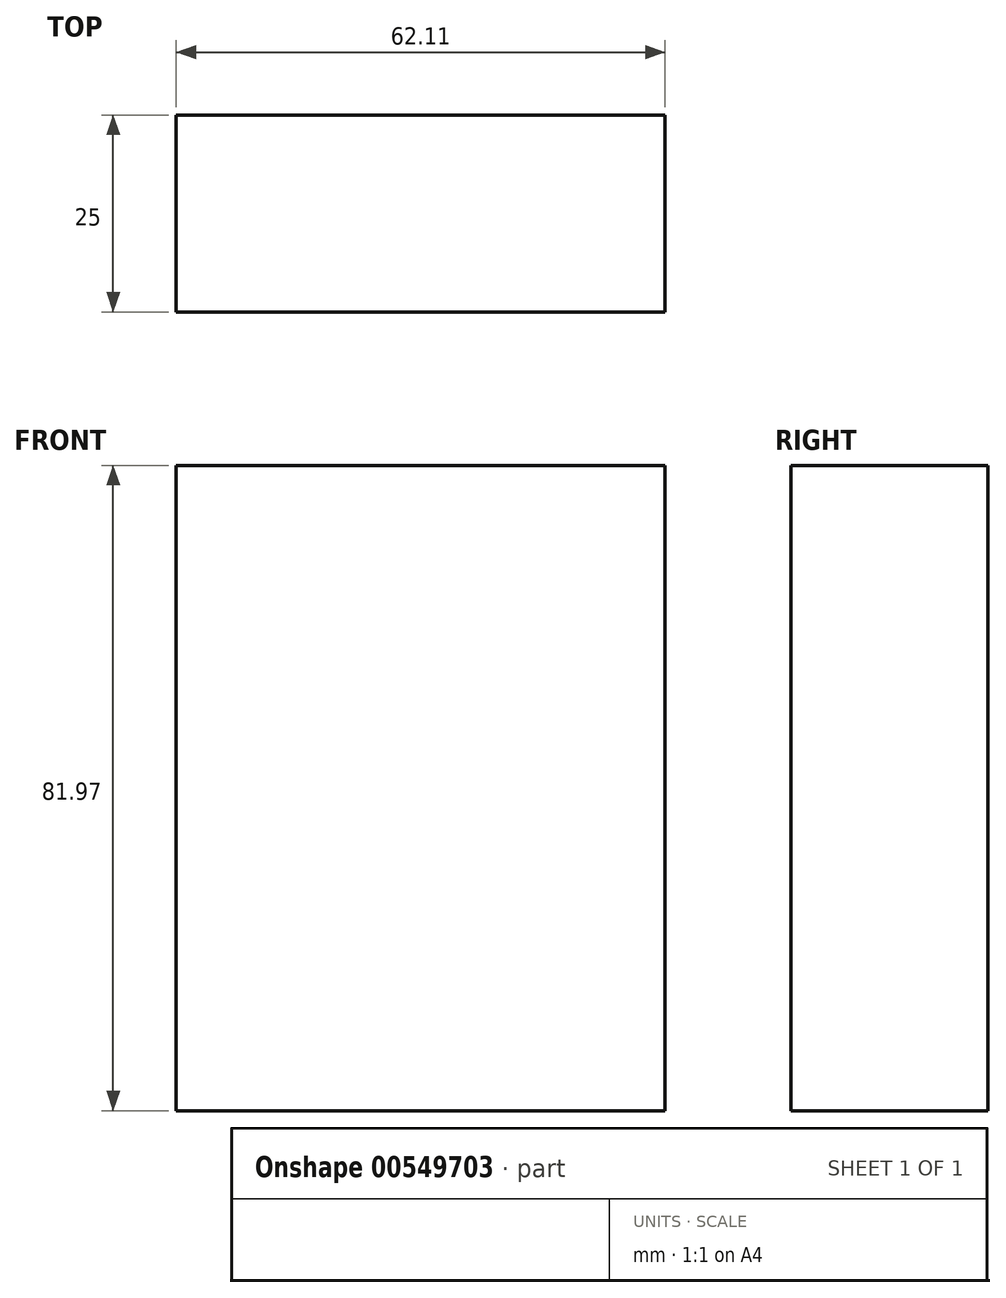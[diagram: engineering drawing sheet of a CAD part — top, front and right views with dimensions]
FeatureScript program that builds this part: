
annotation { "Feature Type Name" : "Feature", "Feature Type Description" : "" }
export const myFeature = defineFeature(function(context is Context, id is Id, definition is map)
    precondition{}
    {
        {
            var Q0;
            Q0=qCreatedBy(makeId("Front.planeOp"),FACE);
            var sketch = newSketch(context, id + "F0", { "sketchPlane" : qUnion([Q0])});
            skLineSegment(sketch, "E0.bottom", {"start": v(-121.8, 69.7) * mm, "end": v(-59.7, 69.7) * mm});
            skLineSegment(sketch, "E0.top", {"start": v(-121.8, -12.28) * mm, "end": v(-59.7, -12.28) * mm});
            skLineSegment(sketch, "E0.left", {"start": v(-121.8, 69.7) * mm, "end": v(-121.8, -12.28) * mm});
            skLineSegment(sketch, "E0.right", {"start": v(-59.7, 69.7) * mm, "end": v(-59.7, -12.28) * mm});
            skSolve(sketch);
        }
        {
            var Q0;
            Q0 = qSketchRegion(id + "F0", true);
            extrude(context, id + "F1", {"entities" : qUnion([Q0]), "depth" : 25 * mm, "offsetDistance" : 25 * mm});
        }
    });
